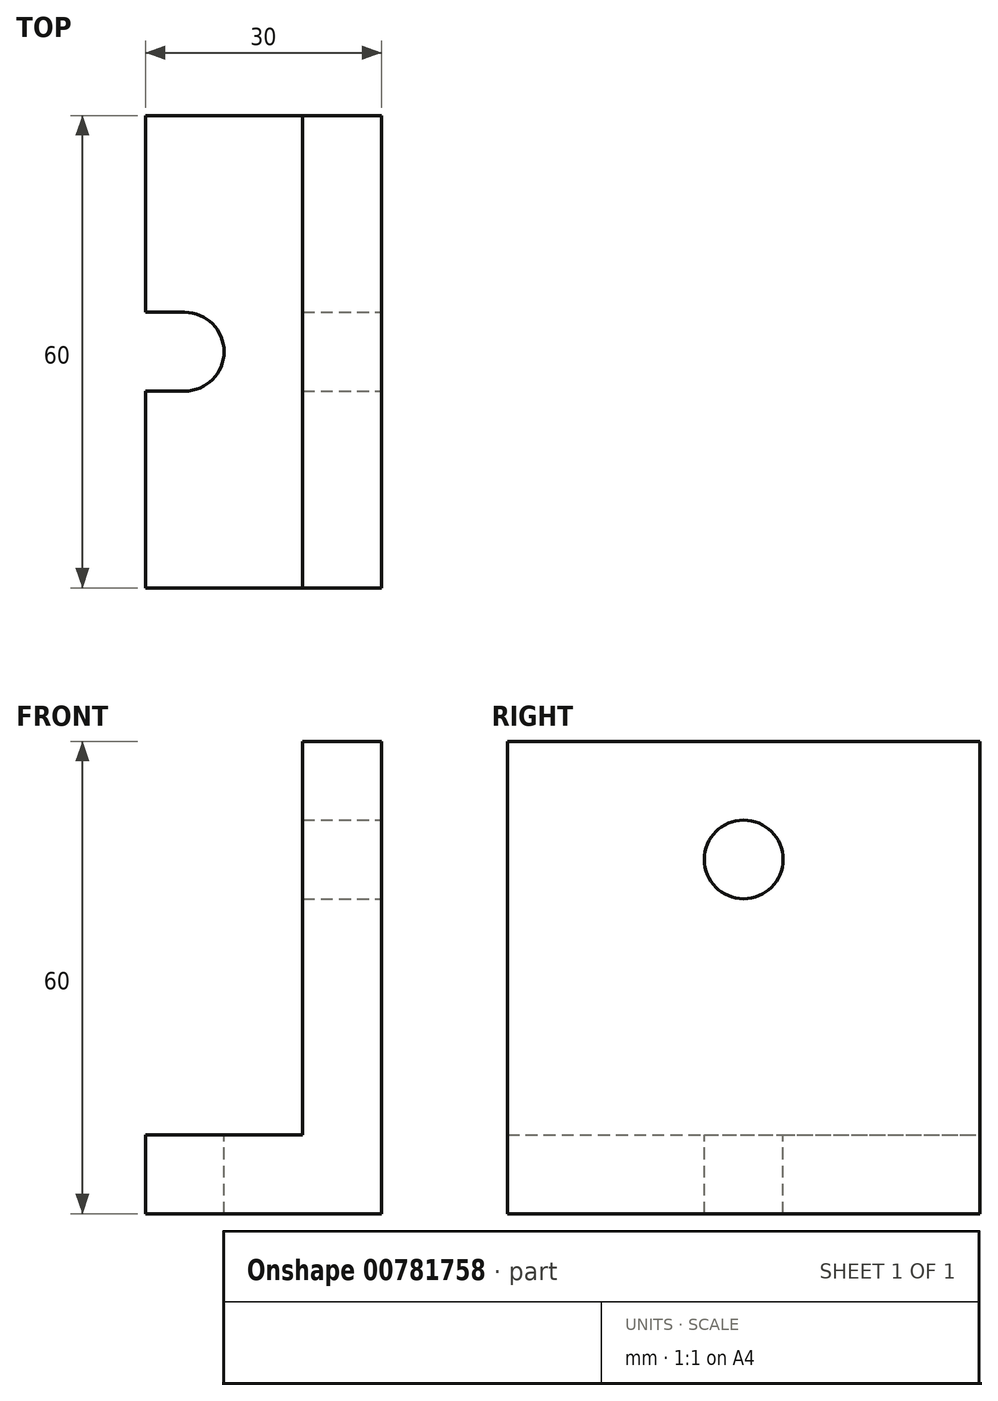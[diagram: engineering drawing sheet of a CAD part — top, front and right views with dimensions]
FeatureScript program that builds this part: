
annotation { "Feature Type Name" : "Feature", "Feature Type Description" : "" }
export const myFeature = defineFeature(function(context is Context, id is Id, definition is map)
    precondition{}
    {
        {
            var Q0;
            Q0=qCreatedBy(makeId("Front.planeOp"),FACE);
            var sketch = newSketch(context, id + "F0", { "sketchPlane" : qUnion([Q0])});
            skLineSegment(sketch, "E0", {"start": v(0, 0) * mm, "end": v(0, 60) * mm});
            skLineSegment(sketch, "E1", {"start": v(0, 60) * mm, "end": v(-10, 60) * mm});
            skLineSegment(sketch, "E2", {"start": v(-10, 60) * mm, "end": v(-10, 10) * mm});
            skLineSegment(sketch, "E3", {"start": v(0, 0) * mm, "end": v(-30, 0) * mm});
            skLineSegment(sketch, "E4", {"start": v(-30, 0) * mm, "end": v(-30, 10) * mm});
            skLineSegment(sketch, "E5", {"start": v(-30, 10) * mm, "end": v(-10, 10) * mm});
            skSolve(sketch);
        }
        {
            var Q0;
            Q0=makeQuery(id+"F0.imprint","IMPRINT",FACE,{"disambiguationData":[TD([[makeQuery(id+"F0.imprint","IMPRINT",EDGE,{"derivedFrom":sQuery(id+"F0.wireOp",EDGE,"E0")}),1.0]])]});
            extrude(context, id + "F1", {"entities" : qUnion([Q0]), "endBound" : BoundingType.SYMMETRIC, "depth" : 60 * mm, "offsetDistance" : 25.4 * mm});
        }
        {
            var Q0;
            Q0=makeQuery(id+"F1.opExtrude","SWEPT_FACE",FACE,{"disambiguationData":[OSD([sQuery(id+"F0.wireOp",EDGE,"E0")])]});
            var sketch = newSketch(context, id + "F2", { "sketchPlane" : qUnion([Q0])});
            skCircle(sketch, "E6", {"center": v(0, 45) * mm, "radius": 5 * mm});
            skSolve(sketch);
        }
        {
            var Q0;
            Q0=makeQuery(id+"F2.imprint","IMPRINT",FACE,{"disambiguationData":[TD([[makeQuery(id+"F2.imprint","IMPRINT",EDGE,{"derivedFrom":sQuery(id+"F2.wireOp",EDGE,"E6")}),1.0]])]});
            extrude(context, id + "F3", {"entities" : qUnion([Q0]), "operationType" : NewBodyOperationType.REMOVE, "oppositeDirection" : true, "depth" : 28.45 * mm, "offsetDistance" : 25.4 * mm});
        }
        {
            var Q0;
            Q0=makeQuery(id+"F1.opExtrude","SWEPT_FACE",FACE,{"disambiguationData":[OSD([sQuery(id+"F0.wireOp",EDGE,"E5")])]});
            var sketch = newSketch(context, id + "F4", { "sketchPlane" : qUnion([Q0])});
            skLineSegment(sketch, "E7", {"start": v(-30, 5) * mm, "end": v(-25, 5) * mm});
            skLineSegment(sketch, "E8", {"start": v(-30, -5) * mm, "end": v(-25, -5) * mm});
            skArc(sketch, "E9", {"start": v(-25, 5) * mm, "mid": v(-20, 0) * mm, "end": v(-25, -5) * mm});
            skSolve(sketch);
        }
        {
            var Q0;
            {var subQ0=sQuery(id+"F4.wireOp",EDGE,"E7");Q0=makeQuery(id+"F4.imprint","IMPRINT",FACE,{"disambiguationData":[TD([[makeQuery(id+"F4.imprint","IMPRINT",EDGE,{"derivedFrom":subQ0}),-1.0]])]});}
            extrude(context, id + "F5", {"entities" : qUnion([Q0]), "operationType" : NewBodyOperationType.REMOVE, "oppositeDirection" : true, "depth" : 25.4 * mm, "offsetDistance" : 25.4 * mm});
        }
        {
            var Q0;
            Q0=qCreatedBy(makeId("Front.planeOp"),FACE);
            cPlane(context, id + "F6", {"entities" : qUnion([Q0]), "cplaneType" : CPlaneType.OFFSET, "offset" : 29.97 * mm, "width" : 152.4 * mm, "height" : 152.4 * mm});
        }
    });
